# Revit family: Emergency_Equipment-Haws_Corporation-Laboratory_Eye_Face_Wash_7610S
name_source: partatom
category: Plumbing Fixtures
revit_build: Autodesk Revit 2016 (Build: 20150220_1215(x64)
units: mm (PartAtom-declared; Revit-internal decimal feet)

## family parameters
Always vertical = Yes
Cut with Voids When Loaded = No
OmniClass Number = 23.45.05.14.24
OmniClass Title = Eye Wash Fountains
Part Type = Normal
Room Calculation Point = No
Round Connector Dimension = Use Radius
Shared = Yes
Work Plane-Based = No

## types (2) — shared parameters
Assembly Code = D2010610
BIMobject category = Other
BIMobject category code = sanitary-sanitary-other
BIMobject main category = Sanitary
BIMobject main category code = sanitary
Brand url = https://www.hawsco.com
CW Connection = Yes
CWFU = 1
Cost = $0.00
Cost Note = For Cost information please visit the Resource tab in the Product Page URL
Date of publishing = 6/4/2019
Description = Extended-length pull down arms are designed to accommodate wheel chair access
Design country = United States
EAN code = https://611970347691
Edition number = 1
Eye Head = Metal - Haws Corporation - Green Powder Coating
Flow = 12 GPM
Goose neck Clearance = 6"
HW Connection = Yes
HWFU = 1
Head Height = 4"
Installation instructions = http://www.hawsco.com
Keynote = 15400
Lever Wide = 10 1/2"
Manufacturer = Haws Corporation 1455 Kleppe Lane Sparks, NV 89431
Manufacturer country = United States
Manufacturer name = Haws Corporation
Masterformat 2014 Code = 22 45 26
Masterformat 2014 Description = Eye/Face Wash Equipment
Material main = Metal
Model = 7610
Nominal height = 14"
Nominal width = 9"
Off Position = Yes
OmniClass Code = 23-29 37 13 15
OmniClass Description = Combination Emergency Eye Wash Stations
On Position = No
Product Documentation Link = http://www.hawsco.com
Product Guid = 216d7893-b5c2-4b38-964f-7053b416086d
Product Page URL = http://www.hawsco.com
Product SKU = haws-7610S
Product certification = http://www.csagroup.org
Product data url = https://bimobject.com
Product family = Eye Wash Fountains
Product group = Emergency Equipment - Showers & Eyewashes - Barrier Free Emergency Equipment
Product url = https://www.hawsco.com
Series = Twin Feather-Flo® heads
Supply Radius = 1/2"
Technical description = http://www.hawsco.com
Type Comments = Pull down eye/face wash are installed in accessible sink
URL = http://www.hawsco.com
Vent Connection = No
WFU = 1
Waste Connection = No
Weight Net (Kg) = 7

## per-type parameters (varying)
| type | Deck Mounted | Wall Mounted |
| 7610S - Wall Mount | No | Yes |
| 7610S - Deck Mount | Yes | No |

## geometry (parser evidence)
native form markers: Blend x18, Sweep x6
no freeform markers — native parametric forms only
